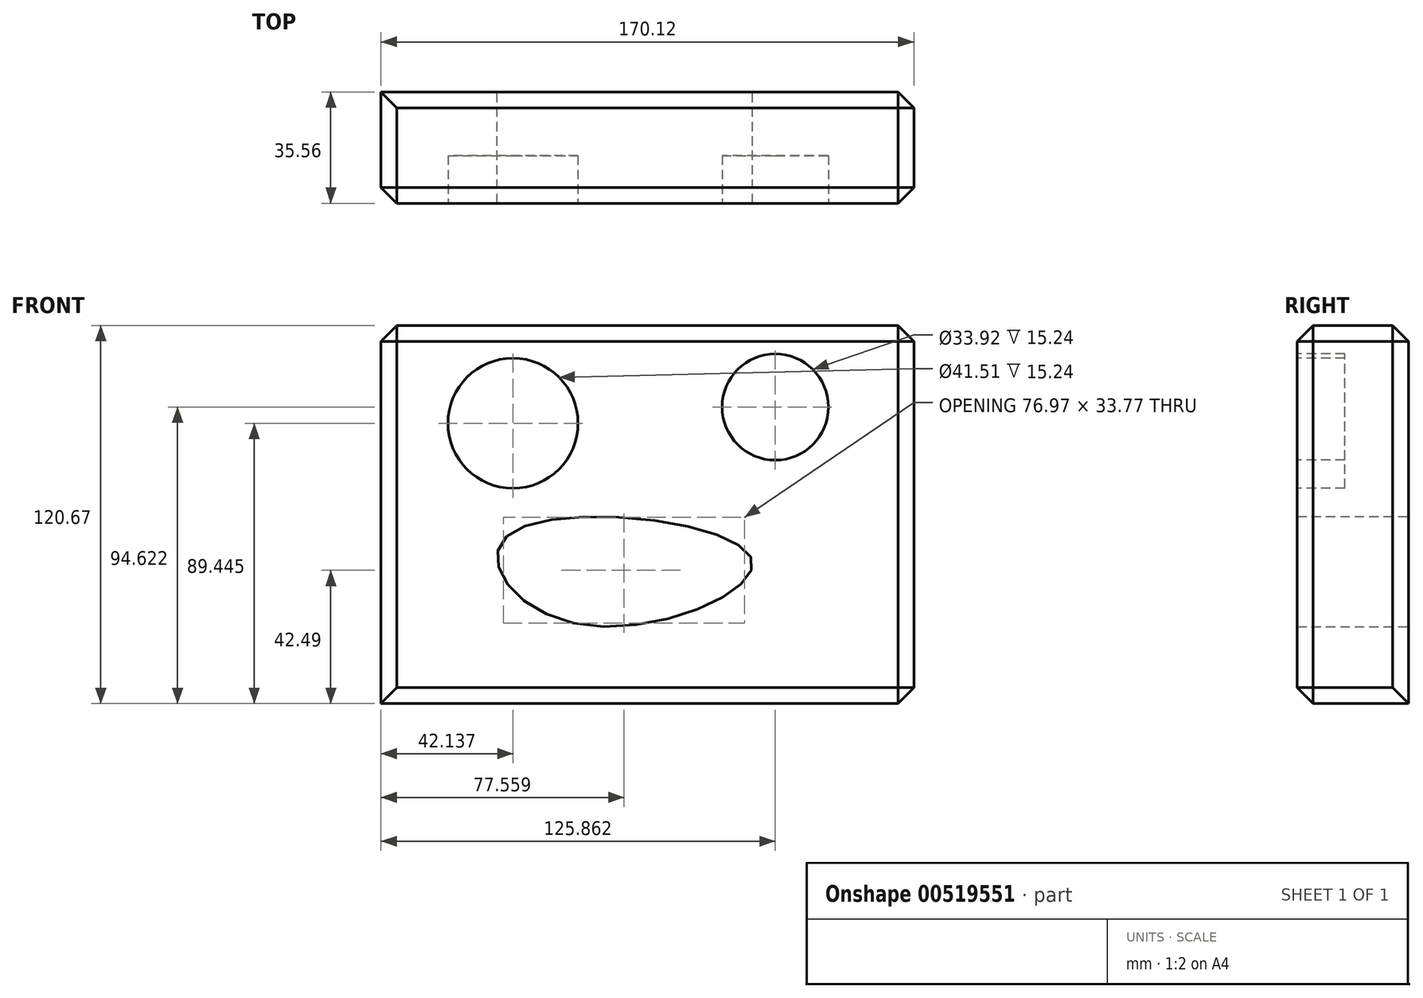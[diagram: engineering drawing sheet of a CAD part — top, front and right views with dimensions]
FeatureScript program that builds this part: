
annotation { "Feature Type Name" : "Feature", "Feature Type Description" : "" }
export const myFeature = defineFeature(function(context is Context, id is Id, definition is map)
    precondition{}
    {
        {
            var Q0;
            Q0=qCreatedBy(makeId("Front.planeOp"),FACE);
            var sketch = newSketch(context, id + "F0", { "sketchPlane" : qUnion([Q0])});
            skLineSegment(sketch, "E0.bottom", {"start": v(-99.22, 43.52) * mm, "end": v(70.9, 43.52) * mm});
            skLineSegment(sketch, "E0.top", {"start": v(-99.22, -77.15) * mm, "end": v(70.9, -77.15) * mm});
            skLineSegment(sketch, "E0.left", {"start": v(-99.22, 43.52) * mm, "end": v(-99.22, -77.15) * mm});
            skLineSegment(sketch, "E0.right", {"start": v(70.9, 43.52) * mm, "end": v(70.9, -77.15) * mm});
            skSolve(sketch);
        }
        {
            var Q0;
            Q0=makeQuery(id+"F0.imprint","IMPRINT",FACE,{"disambiguationData":[TD([[makeQuery(id+"F0.imprint","IMPRINT",EDGE,{"derivedFrom":sQuery(id+"F0.wireOp",EDGE,"E0.bottom")}),-1.0]])]});
            extrude(context, id + "F1", {"entities" : qUnion([Q0]), "depth" : 35.56 * mm, "offsetDistance" : 25.4 * mm});
        }
        {
            var Q0;
            Q0=makeQuery(id+"F1.opExtrude","SWEPT_FACE",FACE,{"disambiguationData":[OSD([sQuery(id+"F0.wireOp",EDGE,"E0.bottom")])]});
            var Q1;
            Q1=makeQuery(id+"F1.opExtrude","CAP_FACE",FACE,{"disambiguationData":[OSD([sQuery(id+"F0.wireOp",EDGE,"E0.bottom"),sQuery(id+"F0.wireOp",EDGE,"E0.top"),sQuery(id+"F0.wireOp",EDGE,"E0.left"),sQuery(id+"F0.wireOp",EDGE,"E0.right")])],"isStart":false});
            var Q2;
            Q2=makeQuery(id+"F1.opExtrude","SWEPT_FACE",FACE,{"disambiguationData":[OSD([sQuery(id+"F0.wireOp",EDGE,"E0.right")])]});
            chamfer(context, id + "F2", {"entities" : qUnion([Q0, Q1, Q2]), "width" : 5.08 * mm, "tangentPropagation" : true});
        }
        {
            var Q0;
            Q0=makeQuery(id+"F1.opExtrude","CAP_FACE",FACE,{"disambiguationData":[OSD([sQuery(id+"F0.wireOp",EDGE,"E0.bottom"),sQuery(id+"F0.wireOp",EDGE,"E0.top"),sQuery(id+"F0.wireOp",EDGE,"E0.left"),sQuery(id+"F0.wireOp",EDGE,"E0.right")])],"isStart":false});
            var sketch = newSketch(context, id + "F3", { "sketchPlane" : qUnion([Q0])});
            skLineSegment(sketch, "E1.bottom", {"start": v(-78, 10.6) * mm, "end": v(-34.8, 10.6) * mm});
            skLineSegment(sketch, "E1.top", {"start": v(-78, -26.6) * mm, "end": v(-34.8, -26.6) * mm});
            skLineSegment(sketch, "E1.left", {"start": v(-78, 10.6) * mm, "end": v(-78, -26.6) * mm});
            skLineSegment(sketch, "E1.right", {"start": v(-34.8, 10.6) * mm, "end": v(-34.8, -26.6) * mm});
            skSolve(sketch);
        }
        {
            var Q0;
            Q0=makeQuery(id+"F3.imprint","IMPRINT",FACE,{"disambiguationData":[TD([[makeQuery(id+"F3.imprint","IMPRINT",EDGE,{"derivedFrom":sQuery(id+"F3.wireOp",EDGE,"E1.bottom")}),-1.0]])]});
            extrude(context, id + "F4", {"entities" : qUnion([Q0]), "operationType" : NewBodyOperationType.ADD, "oppositeDirection" : true, "depth" : 26.42 * mm, "offsetDistance" : 25.4 * mm});
        }
        {
            var Q0;
            Q0=makeQuery(id+"F1.opExtrude","CAP_FACE",FACE,{"disambiguationData":[OSD([sQuery(id+"F0.wireOp",EDGE,"E0.bottom"),sQuery(id+"F0.wireOp",EDGE,"E0.top"),sQuery(id+"F0.wireOp",EDGE,"E0.left"),sQuery(id+"F0.wireOp",EDGE,"E0.right")])],"isStart":false});
            var sketch = newSketch(context, id + "F5", { "sketchPlane" : qUnion([Q0])});
            skCircle(sketch, "E2", {"center": v(-57.08, 12.3) * mm, "radius": 20.75 * mm});
            skCircle(sketch, "E3", {"center": v(26.64, 17.47) * mm, "radius": 16.96 * mm});
            skSolve(sketch);
        }
        {
            var Q0;
            Q0=makeQuery(id+"F5.imprint","IMPRINT",FACE,{"disambiguationData":[TD([[makeQuery(id+"F5.imprint","IMPRINT",EDGE,{"derivedFrom":sQuery(id+"F5.wireOp",EDGE,"E2")}),1.0]])]});
            var Q1;
            Q1=makeQuery(id+"F5.imprint","IMPRINT",FACE,{"disambiguationData":[TD([[makeQuery(id+"F5.imprint","IMPRINT",EDGE,{"derivedFrom":sQuery(id+"F5.wireOp",EDGE,"E3")}),1.0]])]});
            extrude(context, id + "F6", {"entities" : qUnion([Q0, Q1]), "operationType" : NewBodyOperationType.REMOVE, "oppositeDirection" : true, "depth" : 15.24 * mm, "offsetDistance" : 25.4 * mm});
        }
        {
            var Q0;
            Q0=makeQuery(id+"F1.opExtrude","CAP_FACE",FACE,{"disambiguationData":[OSD([sQuery(id+"F0.wireOp",EDGE,"E0.bottom"),sQuery(id+"F0.wireOp",EDGE,"E0.top"),sQuery(id+"F0.wireOp",EDGE,"E0.left"),sQuery(id+"F0.wireOp",EDGE,"E0.right")])],"isStart":false});
            var sketch = newSketch(context, id + "F7", { "sketchPlane" : qUnion([Q0])});
            skFitSpline(sketch, "E4", {"points": [v(-37.84, -51.54) * mm, v(-59, -23.69) * mm, v(18.94, -30.68) * mm, v(-37.84, -51.54) * mm]});
            skSolve(sketch);
        }
        {
            var Q0;
            Q0=makeQuery(id+"F7.imprint","IMPRINT",FACE,{"disambiguationData":[TD([[makeQuery(id+"F7.imprint","IMPRINT",EDGE,{"derivedFrom":sQuery(id+"F7.wireOp",EDGE,"E4")}),-1.0]])]});
            extrude(context, id + "F8", {"entities" : qUnion([Q0]), "operationType" : NewBodyOperationType.REMOVE, "oppositeDirection" : true, "depth" : 45.72 * mm, "offsetDistance" : 25.4 * mm});
        }
    });
